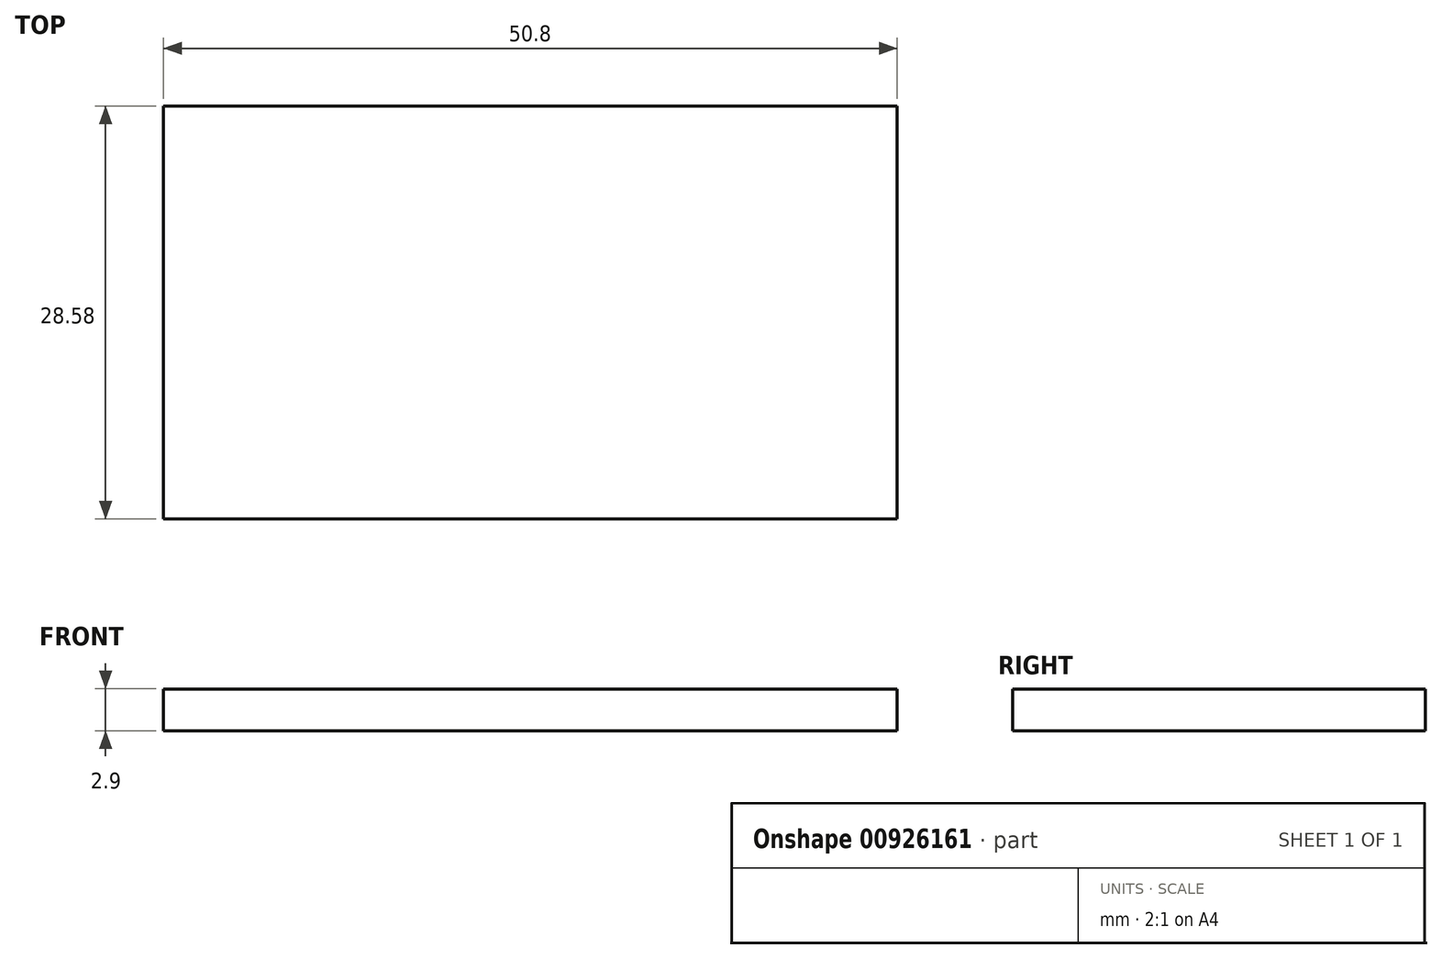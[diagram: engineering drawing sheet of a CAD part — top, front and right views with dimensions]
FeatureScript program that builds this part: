
annotation { "Feature Type Name" : "Feature", "Feature Type Description" : "" }
export const myFeature = defineFeature(function(context is Context, id is Id, definition is map)
    precondition{}
    {
        {
            var Q0;
            Q0=qCreatedBy(makeId("Top.planeOp"),FACE);
            var sketch = newSketch(context, id + "F0", { "sketchPlane" : qUnion([Q0])});
            skLineSegment(sketch, "E0.bottom", {"start": v(25.4, -14.29) * mm, "end": v(-25.4, -14.29) * mm});
            skLineSegment(sketch, "E0.top", {"start": v(25.4, 14.29) * mm, "end": v(-25.4, 14.29) * mm});
            skLineSegment(sketch, "E0.left", {"start": v(25.4, -14.29) * mm, "end": v(25.4, 14.29) * mm});
            skLineSegment(sketch, "E0.right", {"start": v(-25.4, -14.29) * mm, "end": v(-25.4, 14.29) * mm});
            skPoint(sketch, "E0.middle", {"position": v(0, 0) * mm});
            skSolve(sketch);
        }
        {
            var Q0;
            Q0=qSketchRegion(id+"F0",true);
            extrude(context, id + "F1", {"entities" : qUnion([Q0]), "depth" : 2.9 * mm, "offsetDistance" : 25.4 * mm});
        }
    });
